# Revit family: Metal_Lockers-Salsbury_Industries-S_62000_Series-3_Wide_Units
name_source: partatom
category: Specialty Equipment
revit_build: Autodesk Revit 2016 (Build: 20150714_1515(x64)
units: mm (PartAtom-declared; Revit-internal decimal feet)

## family parameters
Always vertical = Yes
Cut with Voids When Loaded = No
OmniClass Number = 23.40.00.00
OmniClass Title = Equipment and Furnishings
Part Type = Normal
Room Calculation Point = No
Round Connector Dimension = Use Diameter
Shared = No
Work Plane-Based = No

## types (18) — shared parameters
Assembly Code = C1030310
Door Window Offset = 4.153 "
Door Window Width = 6.5 "
Hasp Handle Material = Plastic - Salsbury Finish - Black
Hasp Plate Rivet Material = Steel -Salsbury Finish - Polished Steel
Manufacturer = Salsbury Industries
MasterFormat Number = 10 51 13
MasterFormat Title = Lockers
OmniClass 23 Number = 23.40.00.00
Type Comments = See-Through Metal Lockers - Double Tier
URL = www.lockers.com
Version = 3.0 (03/30/18)
Width = 36.04 "
Window Panel Material = Polycarbonate - Salsbury Finish - Clear

## per-type parameters (varying)
| type | Base Height | Compartment Divider Height | Depth | Description | Door Location D1 | Door Window Height | Individual Door Height | Model | OmniClass 23 Title | Sloping Hood Height | Standard Leg Base | Unit Height | Zee Base |
| S-62362 - with Standard 6" High Legs | 6 " | 34.472 " | 12.01 " | 3 Wide - 6 Feet High - 12 Inches Deep | See-Through Metal Locker Doors-12 inch with Hasps : Double Tier Door - 6 foot | 10.25 " | 34.847 " | S-62362 | Equipment and Furnishings | 6.625 " | Metal Locker Legs - 3 Wide : 6" High - 36" W x 12" D | 72 " | Metal Locker Zee Base - 3 Wide : None |
| S-62365 - with Standard 6" High Legs | 6 " | 34.472 " | 15.01 " | 3 Wide - 6 Feet High - 15 Inches Deep | See-Through Metal Locker Doors-12 inch with Hasps : Double Tier Door - 6 foot | 10.25 " | 34.847 " | S-62365 | Equipment and Furnishings | 8.682 " | Metal Locker Legs - 3 Wide : 6" High - 36" W x 15" D | 72 " | Metal Locker Zee Base - 3 Wide : None |
| S-62368 - with Standard 6" High Legs | 6 " | 34.472 " | 18.01 " | 3 Wide - 6 Feet High - 18 Inches Deep | See-Through Metal Locker Doors-12 inch with Hasps : Double Tier Door - 6 foot | 10.25 " | 34.847 " | S-62368 | Equipment and Furnishings | 10.739 " | Metal Locker Legs - 3 Wide : 6" High - 36"W x 18"D | 72 " | Metal Locker Zee Base - 3 Wide : None |
| S-62362 - with 77572 Zee Base and 77550 Lockers without Legs | 4 " | 34.472 " | 12.01 " | 3 Wide - 6 Feet High - 12 Inches Deep with Zee Base and Lockers without Legs | See-Through Metal Locker Doors-12 inch with Hasps : Double Tier Door - 6 foot | 10.25 " | 34.847 " | S-62362 with 77572 and 77550 | Equipment and Furnishings | 6.625 " | Metal Locker Legs - 3 Wide : No Legs | 72 " | Metal Locker Zee Base - 3 Wide : 77572- 36" W x 12" D |
| S-62365 - with 77575 Zee Base and 77550 Lockers without Legs | 4 " | 34.472 " | 15.01 " | 3 Wide - 6 Feet High - 15 Inches Deep with Zee Base and Lockers without Legs | See-Through Metal Locker Doors-12 inch with Hasps : Double Tier Door - 6 foot | 10.25 " | 34.847 " | S-62365 with 77575 and 77550 | Equipment and Furnishings | 8.682 " | Metal Locker Zee Base - 3 Wide : None | 72 " | Metal Locker Zee Base - 3 Wide : 77575 - 36" W x 15" D |
| S-62368 - with 77578 Zee Base and 77550 Lockers without Legs | 4 " | 34.472 " | 18.01 " | 3 Wide - 6 Feet High - 18 Inches Deep with Zee Base and Lockers without Legs | See-Through Metal Locker Doors-12 inch with Hasps : Double Tier Door - 6 foot | 10.25 " | 34.847 " | S-62368 with 77578 and 77550 | Equipment aqnd Furnishings | 10.739 " | Metal Locker Zee Base - 3 Wide : None | 72 " | Metal Locker Zee Base - 3 Wide : 77578 - 36"W x 18"D |
| S-62362 - with 77550 Lockers without Legs | 0 " | 34.472 " | 12.01 " | 3 Wide - 6 Feet High - 12 Inches Deep with Lockers without Legs | See-Through Metal Locker Doors-12 inch with Hasps : Double Tier Door - 6 foot | 10.25 " | 34.847 " | S-62362 with 77550 | Equipment and Furnishings | 6.625 " | Metal Locker Legs - 3 Wide : No Legs | 72 " | Metal Locker Zee Base - 3 Wide : None |
| S-62365 - with 77550 Lockers without Legs | 0 " | 34.472 " | 15.01 " | 3 Wide - 6 Feet High - 15 Inches Deep with Lockers without Legs | See-Through Metal Locker Doors-12 inch with Hasps : Double Tier Door - 6 foot | 10.25 " | 34.847 " | S-62365 with 77550 | Equipment and Furnishings | 8.682 " | Metal Locker Legs - 3 Wide : No Legs | 72 " | Metal Locker Zee Base - 3 Wide : None |
| S-62368 - with 77550 Lockers without Legs | 0 " | 34.472 " | 18.01 " | 3 Wide - 6 Feet High - 18 Inches Deep with Lockers without Legs | See-Through Metal Locker Doors-12 inch with Hasps : Double Tier Door - 6 foot | 10.25 " | 34.847 " | S-62368 with 77550 | Equipment and Furnishings | 10.739 " | Metal Locker Legs - 3 Wide : No Legs | 72 " | Metal Locker Zee Base - 3 Wide : None |
| S-62352 - with Standard 6" High Legs | 6 " | 28.472 " | 12.01 " | 3 Wide - 5 Feet High - 12 Inches Deep | See-Through Metal Locker Doors-12 inch with Hasps : Double Tier Door - 5 feet | 7.25 " | 28.847 " | S-62352 | Equipment and Furnishings | 6.625 " | Metal Locker Legs - 3 Wide : 6" High - 36" W x 12" D | 60 " | Metal Locker Zee Base - 3 Wide : None |
| S-62352 - with 77572 Zee Base and 77550 Lockers without Legs | 4 " | 28.472 " | 12.01 " | 3 Wide - 5 Feet High - 12 Inches Deep with Zee Base and Lockers without Legs | See-Through Metal Locker Doors-12 inch with Hasps : Double Tier Door - 5 feet | 7.25 " | 28.847 " | S-62352 with 77572 and 77550 | Equipment and Furnishings | 6.625 " | Metal Locker Zee Base - 3 Wide : None | 60 " | Metal Locker Zee Base - 3 Wide : 77572- 36" W x 12" D |
| S-62352 - with 77550 Lockers without Legs | 0 " | 28.472 " | 12.01 " | 3 Wide - 5 Feet High - 12 Inches Deep with Lockers without Legs | See-Through Metal Locker Doors-12 inch with Hasps : Double Tier Door - 5 feet | 7.25 " | 28.847 " | S-62352 with 77550 | Equipment and Furnishings | 6.625 " | Metal Locker Legs - 3 Wide : No Legs | 60 " | Metal Locker Zee Base - 3 Wide : None |
| S-62355 - with Standard 6" High Legs | 6 " | 28.472 " | 15.01 " | 3 Wide - 5 Feet High - 15 Inches Deep | See-Through Metal Locker Doors-12 inch with Hasps : Double Tier Door - 5 feet | 7.25 " | 28.847 " | S-62355 | Equipment and Furnishings | 8.682 " | Metal Locker Legs - 3 Wide : 6" High - 36" W x 15" D | 60 " | Metal Locker Zee Base - 3 Wide : None |
| S-62355 - with 77575 Zee Base and 77550 Lockers without Legs | 4 " | 28.472 " | 15.01 " | 3 Wide - 5 Feet High - 15 Inches Deep with Zee Base and Lockers without Legs | See-Through Metal Locker Doors-12 inch with Hasps : Double Tier Door - 5 feet | 7.25 " | 28.847 " | S-62355 with 77575 and 77550 | Equipment and Furnishings | 8.682 " | Metal Locker Zee Base - 3 Wide : None | 60 " | Metal Locker Zee Base - 3 Wide : 77575 - 36" W x 15" D |
| S-62355 - with 77550 Lockers without Legs | 0 " | 28.472 " | 15.01 " | 3 Wide - 5 Feet High - 15 Inches Deep with Lockers without Legs | See-Through Metal Locker Doors-12 inch with Hasps : Double Tier Door - 5 feet | 7.25 " | 28.847 " | S-62355 with 77550 | Equipment and Furnishings | 8.682 " | Metal Locker Legs - 3 Wide : No Legs | 60 " | Metal Locker Zee Base - 3 Wide : None |
| S-62358 - with Standard 6" High Legs | 6 " | 28.472 " | 18.01 " | 3 Wide - 5 Feet High - 18 Inches Deep | See-Through Metal Locker Doors-12 inch with Hasps : Double Tier Door - 5 feet | 7.25 " | 28.847 " | S-62358 | Equipment and Furnishings | 10.739 " | Metal Locker Legs - 3 Wide : 6" High - 36"W x 18"D | 60 " | Metal Locker Zee Base - 3 Wide : None |
| S-62358 - with 77578 Zee Base and 77550 Lockers without Legs | 4 " | 28.472 " | 18.01 " | 3 Wide - 5 Feet High - 18 Inches Deep with Zee Base and Lockers without Legs | See-Through Metal Locker Doors-12 inch with Hasps : Double Tier Door - 5 feet | 7.25 " | 28.847 " | S-62358 with 77578 and 77550 | Equipment and Furnishings | 10.739 " | Metal Locker Zee Base - 3 Wide : None | 60 " | Metal Locker Zee Base - 3 Wide : 77578 - 36"W x 18"D |
| S-62358 - with 77550 Lockers without Legs | 0 " | 28.472 " | 18.01 " | 3 Wide - 5 Feet High - 18 Inches Deep with Lockers without Legs | See-Through Metal Locker Doors-12 inch with Hasps : Double Tier Door - 5 feet | 7.25 " | 28.847 " | S-62358 with 77550 | Equipment and Furnishings | 10.739 " | Metal Locker Legs - 3 Wide : No Legs | 60 " | Metal Locker Zee Base - 3 Wide : None |

## geometry (parser evidence)
native form markers: Sweep x37
no freeform markers — native parametric forms only
